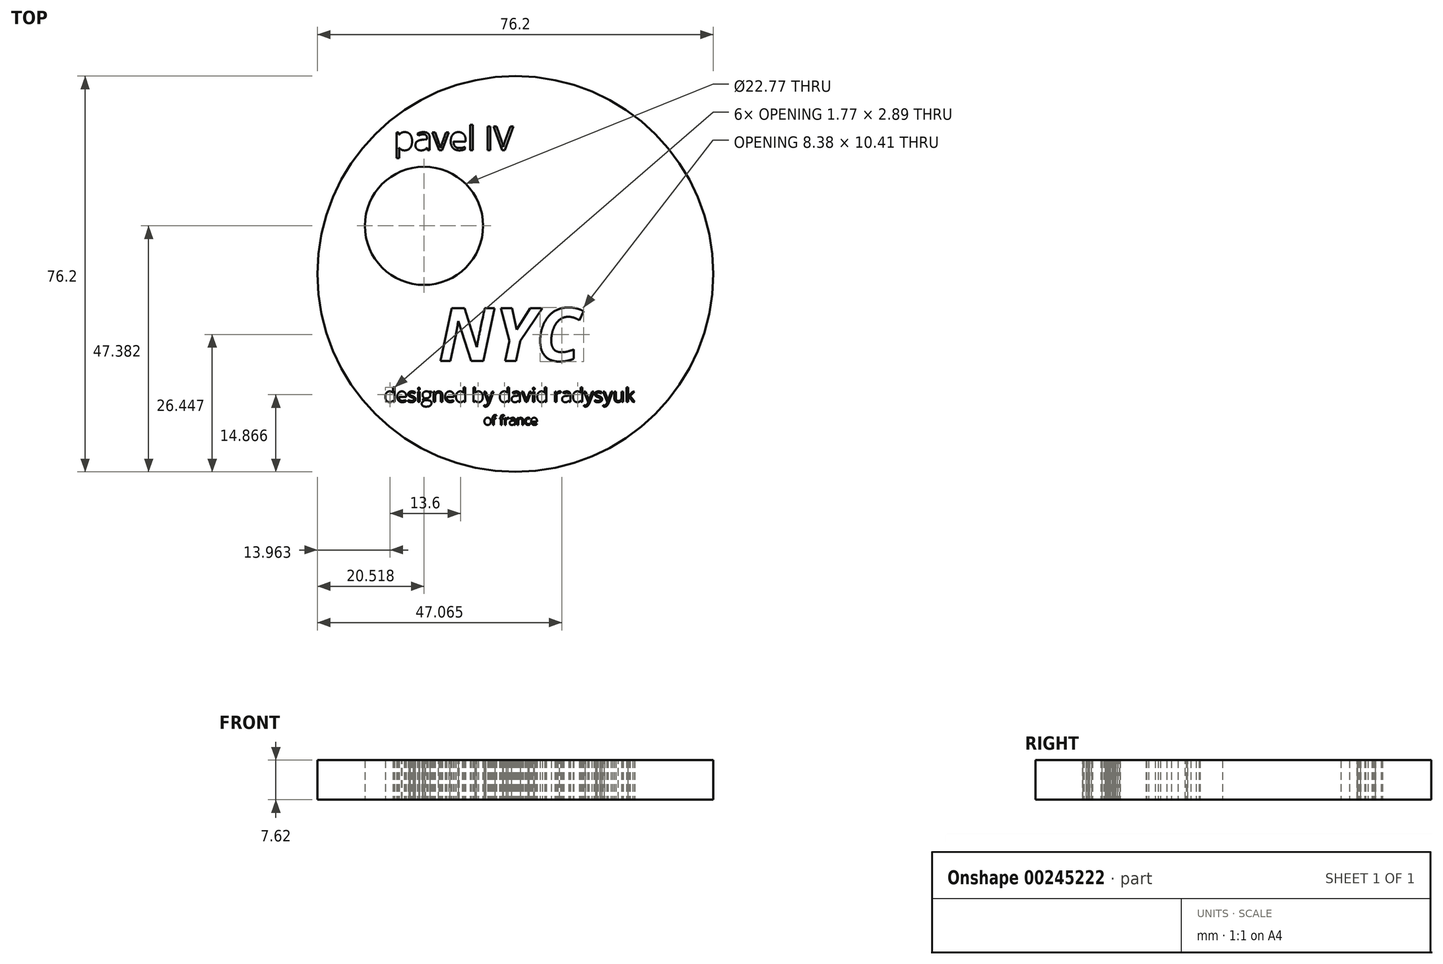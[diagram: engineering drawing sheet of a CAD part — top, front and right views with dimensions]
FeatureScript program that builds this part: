
annotation { "Feature Type Name" : "Feature", "Feature Type Description" : "" }
export const myFeature = defineFeature(function(context is Context, id is Id, definition is map)
    precondition{}
    {
        {
            var Q0;
            Q0=qCreatedBy(makeId("Top.planeOp"),FACE);
            var sketch = newSketch(context, id + "F0", { "sketchPlane" : qUnion([Q0])});
            skCircle(sketch, "E0", {"center": v(-17.58, 9.28) * mm, "radius": 11.38 * mm});
            skCircle(sketch, "E1", {"center": v(0, 0) * mm, "radius": 38.1 * mm});
            skText(sketch, "E2", { "text": "NYC\n", "fontName": "OpenSans-BoldItalic.ttf"});
            skText(sketch, "E3", { "text": "designed by david radysyuk", "fontName": "OpenSans-Regular.ttf"});
            skText(sketch, "E4", { "text": "of france\n", "fontName": "OpenSans-Regular.ttf"});
            skText(sketch, "E5", { "text": "pavel IV", "fontName": "OpenSans-Regular.ttf"});
            const initialGuessF0  = {"E2": [-0.01476, -0.01672, 1, 0, 0.0102], "E3": [-0.02523, -0.02464, 1, 0, 0.0027], "E4": [-0.00609, -0.02904, 1, 0, 0.0018], "E5": [-0.02342, 0.02386, 1, 0, 0.00458]};
            skSetInitialGuess(sketch, initialGuessF0);
            skSolve(sketch);
        }
        {
            var Q0;
            Q0=makeQuery(id+"F0.imprint","IMPRINT",FACE,{"disambiguationData":[TD([[makeQuery(id+"F0.imprint","IMPRINT",EDGE,{"derivedFrom":sQuery(id+"F0.wireOp",EDGE,"E0")}),-1.0]])]});
            extrude(context, id + "F1", {"entities" : qUnion([Q0]), "depth" : 7.62 * mm});
        }
    });
